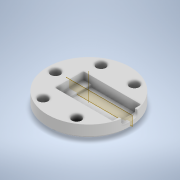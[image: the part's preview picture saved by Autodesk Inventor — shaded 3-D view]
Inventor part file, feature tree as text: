
AUTODESK INVENTOR PART (.ipt)
format: ipt  version: 2021 (Build 250183000, 183)  size: 854,016 bytes
history: native  units: in
note: dims shown in document units (in); Inventor stores cm internally (conversion verified against a paired STEP export)
features: extrude x7, sketch x7, fillet x3, chamfer x1, other x1, plane x1, pattern_circular x1
ambient origin geometry x8: Origin, YZ Plane, XZ Plane, XY Plane, X Axis, Y Axis, Z Axis, Center Point
bodies: Solid1 (feature_tree)
feature tree (21):
  extrude  "Extrusion1"  Depth=0.315in TaperAngle=0.0deg
  chamfer  "Chamfer2"  Distance=0.189in
  extrude  "Extrusion2"  Depth=0.1575in
  extrude  "Extrusion3"  Depth=0.2205in
  other  "Work Axis1"
  plane  "Work Plane1"
  extrude  "Extrusion5"  Depth=0.2047in TaperAngle=0.0deg
  extrude  "Extrusion4"  Depth=0.8268in
  fillet  "Fillet4"  Radius=0.3539in
  pattern_circular  "Circular Pattern2"  [2 undecoded]
  fillet  "Fillet7"  Radius=0.063in
  extrude  "Extrusion9"  Depth=0.1575in
  extrude  "Extrusion10"  Depth=0.0394in
  fillet  "Fillet9"  [1 undecoded]
  sketch  "Sketch1"  dims[d0=2.0472in d3=0.315in d4=0.0in]
  sketch  "Sketch2"  dims[d5=1.4315in]
  sketch  "Sketch3"  dims[d6=0.7079in]
  sketch  "Sketch4"  dims[d7=0.3539in]
  sketch  "Sketch7"  dims[d8=0.4882in d9=0.189in d10=0.0in]
  sketch  "Sketch12"  dims[d11=0.0in d14=0.1575in]
  sketch  "Sketch13"  dims[d15=0.0in d16=0.0in d17=0.2205in d18=0.2047in d19=0.0in d23=0.8268in d24=0.3539in d31=0.1969in d32=0.063in d33=0.0in d44=0.1575in d47=0.0394in d48=0.0in d49=0.0in d51=0.0in d54=0.063in d55=0.0in d56=45.0deg d58=0.0394in d59=0.1181in d60=1.9685in d61=240.0deg d72=0.0315in d80=1.1811in d81=0.5906in d82=0.9728in d83=0.4864in d84=0.0394in d85=0.0in d86=0.547in d87=0.2735in d88=0.0787in d89=0.0in d90=0.0787in d98=0.1024in d99=0.0in d100=0.0in d91=0.0197in d92=0.0344in d93=0.0197in d94=0.0344in]
note: 3 required parameter values undecoded (feature->parameter linkage not recoverable at this tier; creation-order binding heuristic only, values carry confidence <= 0.55)
